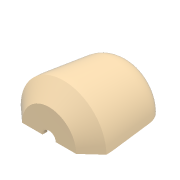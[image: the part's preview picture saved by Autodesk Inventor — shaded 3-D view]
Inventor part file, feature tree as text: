
AUTODESK INVENTOR PART (.ipt)
format: ipt  version: 2017 (Build 210142000, 142)  size: 440,832 bytes
history: native  units: mm
features: sketch x16, extrude x11, projected_geometry x5, fillet x4, chamfer x2, plane x2, revolve x1, thicken_offset x1, shell x1
ambient origin geometry x8: Origin, YZ Plane, XZ Plane, XY Plane, X Axis, Y Axis, Z Axis, Center Point
bodies: Solid1 (feature_tree)
feature tree (43):
  revolve  "Revolution1"  [1 undecoded]
  fillet  "Fillet1"  Radius=30.0mm
  chamfer  "Chamfer1"  Distance=10.0mm Angle=45.0deg
  fillet  "Fillet2"  Radius=20.0mm
  fillet  "Fillet3"  Radius=60.0mm
  thicken_offset  "Thicken1"
  extrude  "Extrusion1"  Depth=4.0mm
  sketch  "Sketch3"  dims[d4=20.0mm d5=10.0mm d6=20.0mm d7=45.0deg d8=20.0mm d9=60.0mm]
  extrude  "Extrusion5"  Depth=50.0mm
  sketch  "Sketch7"  dims[d12=0.0mm d13=0.0mm d14=50.0mm]
  plane  "Work Plane1"
  extrude  "Extrusion6"  Depth=12.0mm
  extrude  "Extrusion7"  Depth=12.0mm
  extrude  "Extrusion8"  Depth=40.0mm
  plane  "Work Plane2"
  extrude  "Extrusion9"  Depth=22.0mm
  sketch  "Sketch12"  dims[d39=4.0mm d40=6.0mm]
  extrude  "Extrusion10"  Depth=6.0mm
  extrude  "Extrusion11"  Depth=20.5mm TaperAngle=0.0deg
  chamfer  "Chamfer2"  Distance=6.0mm
  shell  "Shell2"  Thickness=12.0mm
  extrude  "Extrusion12"  Depth=2.0mm TaperAngle=0.0deg
  extrude  "Extrusion13"  Depth=2.0mm TaperAngle=0.0deg
  sketch  "Sketch17"  dims[d55=10.0mm d56=0.0mm d57=0.0mm]
  extrude  "Extrusion14"  TaperAngle=0.0deg  [1 undecoded]
  fillet  "Fillet8"  Radius=2.0mm
  sketch  "Sketch1"  dims[d0=40.0mm d1=80.0mm d2=30.0mm]
  sketch  "Sketch2"  dims[d3=90.0deg]
  sketch  "Sketch6"  dims[d10=4.0mm d11=4.0mm]
  sketch  "Sketch8"  dims[d15=12.0mm d16=12.0mm]
  sketch  "Sketch9"  dims[d17=12.0mm d18=12.0mm]
  projected_geometry  "Projected Loop1"
  sketch  "Sketch10"  dims[d34=45.0mm d35=40.0mm]
  projected_geometry  "Projected Loop2"
  sketch  "Sketch11"  dims[d36=40.0mm d37=0.0mm d38=22.0mm]
  sketch  "Sketch13"  dims[d41=-8.0mm d42=20.5mm d43=0.0mm]
  sketch  "Sketch14"  dims[d44=25.0mm d45=6.0mm d46=0.0mm d47=12.0mm d48=0.0mm]
  sketch  "Sketch15"  dims[d49=-3.75mm d50=2.0mm d51=0.0mm]
  projected_geometry  "Projected Loop3"
  sketch  "Sketch16"  dims[d52=28.0mm d53=2.0mm d54=0.0mm]
  projected_geometry  "Projected Loop4"
  sketch  "Sketch18"  dims[d58=11.0mm d59=2.0mm d60=45.0deg d61=2.0mm d62=10.0mm d63=0.0mm d64=10.0mm d65=0.0mm d66=10.0mm d67=0.0mm d68=3.0mm]
  projected_geometry  "Projected Loop5"
note: 2 required parameter values undecoded (feature->parameter linkage not recoverable at this tier; creation-order binding heuristic only, values carry confidence <= 0.55)